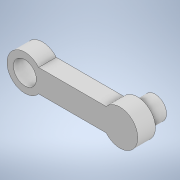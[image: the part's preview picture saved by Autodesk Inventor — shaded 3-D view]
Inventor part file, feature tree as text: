
AUTODESK INVENTOR PART (.ipt)
format: ipt  version: 2022 (Build 260153000, 153)  size: 124,928 bytes
history: native  units: in
note: dims shown in document units (in); Inventor stores cm internally (conversion verified against a paired STEP export)
features: extrude x2, sketch x1
ambient origin geometry x8: Origin, YZ Plane, XZ Plane, XY Plane, X Axis, Y Axis, Z Axis, Center Point
bodies: Body1 (feature_tree)
feature tree (3):
  sketch  "Sketch2"  dims[d4=0.1969in d5=0.0in d6=0.1969in d7=0.0in d8=1.063in d9=0.2559in d10=0.2559in]
  extrude  "Extrusion3"  Depth=0.1969in TaperAngle=0.0deg
  extrude  "Extrusion4"  Depth=0.2559in
